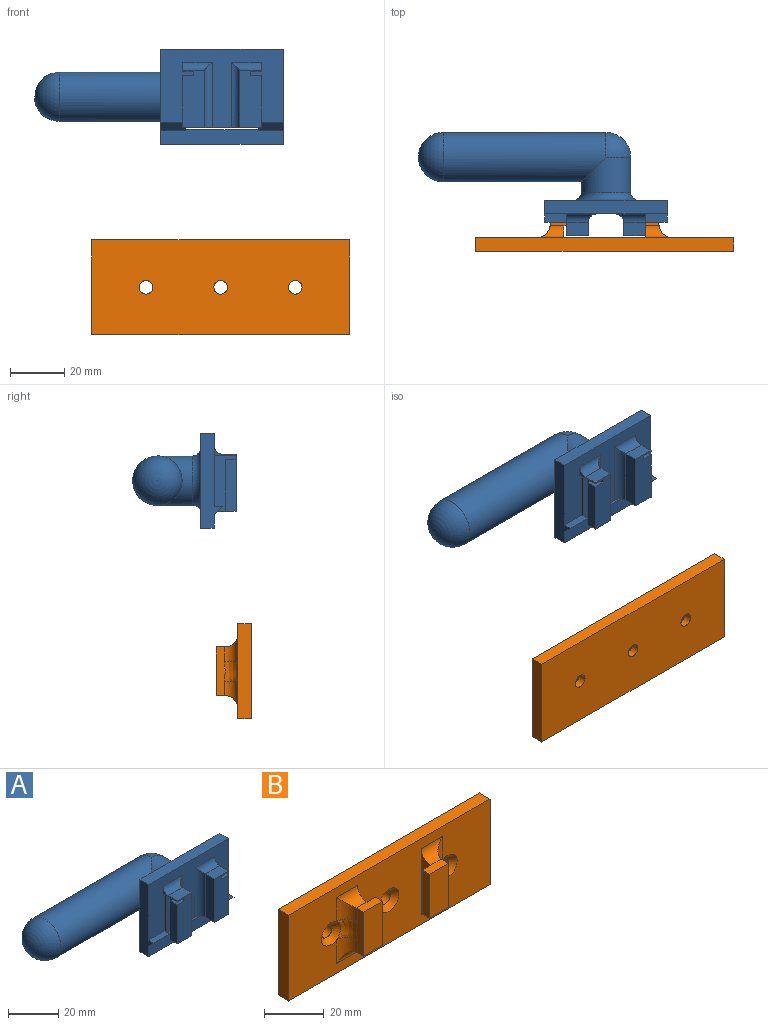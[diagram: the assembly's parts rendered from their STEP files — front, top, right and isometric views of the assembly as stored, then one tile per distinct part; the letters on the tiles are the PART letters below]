
ASSEMBLY  parts=2 mates=1
PART A: 52 faces, bbox 91.7x38.2x35.1 mm
  f0: plane 45x35mm, normal (0,1,0), area 1055.3mm2, adj f9,f10,f11,f12,f15,f20,f21,f22
  f1: plane 21x8mm, normal (0,-1,0), area 162.4mm2, adj f2,f7,f15,f17,f19,f39,f40,f41
  f2: plane 8x5.1mm, normal (0,0,1), area 40.8mm2, adj f1,f17,f41,f50
  f3: plane 19x4mm, normal (1,0,0), area 76mm2, adj f4,f15,f16,f36
  f4: plane 19x4mm, normal (0,1,0), area 76mm2, adj f3,f8,f15,f36
  f5: plane 45x5.75mm, normal (0,-1,0), area 232.2mm2, adj f9,f10,f12,f20,f27,f28,f29,f30
  f6: plane 45x28.75mm, normal (0,-1,0), area 859.3mm2, adj f7,f8,f10,f11,f12,f15,f20,f21
  f7: plane 20.4x8.1mm, normal (-1,0,0), area 89.2mm2, adj f1,f6,f15,f18,f39,f40
  f8: plane 20.45x8.1mm, normal (1,0,0), area 89.6mm2, adj f4,f6,f15,f16,f36,f37
  f9: plane 45x5mm, normal (0,0,-1), area 225mm2, adj f0,f5,f10,f12
  f10: plane 35x8mm, normal (1,0,0), area 179.5mm2, adj f0,f5,f6,f9,f11,f33,f34
  f11: plane 45x5mm, normal (0,0,1), area 225mm2, adj f0,f6,f10,f12
  f12: plane 35x8mm, normal (-1,0,0), area 179.5mm2, adj f0,f5,f6,f9,f11,f31,f32,f35
  f13: plane 8x5.1mm, normal (0,0,1), area 40.8mm2, adj f14,f16,f38,f48
  f14: plane 21x5.1mm, normal (-1,0,0), area 107.1mm2, adj f13,f15,f16,f49
  f15: plane 29.09x13.19mm, normal (0,0,-1), area 220.7mm2, adj f0,f1,f3,f4,f6,f7,f8,f14
  f16: plane 21x8mm, normal (0,-1,0), area 162.2mm2, adj f3,f8,f13,f14,f15,f36,f37,f38
  f17: plane 21x5.1mm, normal (1,0,0), area 107.1mm2, adj f1,f2,f15,f51
  f18: plane 19x4mm, normal (0,1,0), area 76mm2, adj f7,f15,f19,f39
  f19: plane 19x4mm, normal (-1,0,0), area 76mm2, adj f1,f15,f18,f39
  f20: plane 19.73x8mm, normal (-1,0,0), area 99.5mm2, adj f0,f5,f6,f21,f30,f33,f34
  f21: cylinder r=0.5mm len=5mm, axis (0,-1,0), area 7.9mm2, adj f0,f6,f20,f22
  f22: plane 18x5mm, normal (1,0,0), area 90mm2, adj f0,f6,f21,f23
  f23: cylinder r=0.5mm len=5mm, axis (0,-1,0), area 3.9mm2, adj f0,f6,f15,f22
  f24: cylinder r=0.5mm len=5mm, axis (0,-1,0), area 3.9mm2, adj f0,f6,f15,f25
  f25: plane 18x5mm, normal (-1,0,0), area 90mm2, adj f0,f6,f24,f26
  f26: cylinder r=0.5mm len=5mm, axis (0,-1,0), area 7.9mm2, adj f0,f6,f25,f27
  f27: plane 19.74x8mm, normal (1,0,0), area 99.5mm2, adj f0,f5,f6,f26,f28,f31,f32,f35
  f28: cylinder r=0.5mm len=5mm, axis (0,-1,0), area 3.9mm2, adj f0,f5,f27,f29
  f29: plane 26x5mm, normal (0,0,1), area 130mm2, adj f0,f5,f28,f30
  f30: cylinder r=0.5mm len=5mm, axis (0,-1,0), area 3.9mm2, adj f0,f5,f20,f29
  f31: plane 9x3mm, normal (0,0,1), area 27mm2, adj f6,f12,f27,f32
  f32: plane 9x0.01mm, normal (0,-1,0), area 0.1mm2, adj f12,f27,f31,f35
  f33: plane 9x3mm, normal (0,0,1), area 27mm2, adj f6,f10,f20,f34
  f34: plane 9x3mm, normal (0,-0.71,-0.71), area 38.2mm2, adj f5,f10,f20,f33
  f35: plane 9x3mm, normal (0,-0.71,-0.71), area 38.2mm2, adj f5,f12,f27,f32
  f36: plane 4x4mm, normal (0,0,1), area 16mm2, adj f3,f4,f8,f16
  f37: plane 8.1x4mm, normal (0,0,-1), area 32.4mm2, adj f6,f8,f16,f38
  f38: plane 8.1x3.55mm, normal (1,0,0), area 6.4mm2, adj f6,f13,f16,f37,f48
  f39: plane 4x4mm, normal (0,0,1), area 16mm2, adj f1,f7,f18,f19
  f40: plane 8.1x4mm, normal (0,0,-1), area 32.4mm2, adj f1,f6,f7,f41
  f41: plane 8.1x3.6mm, normal (-1,0,0), area 6.8mm2, adj f1,f2,f6,f40,f50
  f42: sphere r=9.1mm, area 260.2mm2, adj f43,f44
  f43: cylinder r=9.1mm len=18.2mm, axis (0,-1,0), area 572.4mm2, adj f42,f44,f46,f47
  f44: cylinder r=9.1mm len=60mm, axis (1,0,0), area 3265mm2, adj f42,f43,f45
  f45: sphere r=9.1mm, area 520.3mm2, adj f44
  f46: torus R=12.1mm, axis (0,-1,0), area 265.5mm2, adj f0,f43,f47
  f47: bspline ~10.45x3.38mm, area 31.1mm2, adj f15,f43,f46
  f48: cylinder r=3mm len=11mm, axis (-1,0,0), area 42.8mm2, adj f6,f13,f38,f49
  f49: cylinder r=3mm len=24mm, axis (0,0,-1), area 104.1mm2, adj f6,f14,f15,f48
  f50: cylinder r=3mm len=11mm, axis (-1,0,0), area 42.8mm2, adj f2,f6,f41,f51
  f51: cylinder r=3mm len=24mm, axis (0,0,1), area 104.1mm2, adj f6,f15,f17,f50
PART B: 36 faces, bbox 95x13x35 mm
  f0: plane 18x9mm, normal (0,-1,0), area 162mm2, adj f7,f9,f29,f31
  f1: plane 18x3.4mm, normal (1,0,0), area 61.2mm2, adj f4,f6,f28,f30
  f2: plane 27x4.6mm, normal (1,0,0), area 91.5mm2, adj f4,f12,f28,f30,f33,f35
  f3: plane 18x3.42mm, normal (-1,0,0), area 55.5mm2, adj f5,f6,f26,f27,f28,f30
  f4: plane 18x4mm, normal (0,1,0), area 72mm2, adj f1,f2,f28,f30
  f5: cylinder r=5mm len=9.76mm, axis (0,0,-1), area 53.4mm2, adj f3,f12,f27,f30,f33
  f6: plane 18x9mm, normal (0,-1,0), area 162mm2, adj f1,f3,f28,f30
  f7: plane 18x3.5mm, normal (-1,0,0), area 63mm2, adj f0,f10,f29,f31
  f8: plane 27x4.5mm, normal (-1,0,0), area 89.7mm2, adj f10,f12,f32,f34
  f9: plane 18x3.42mm, normal (1,0,0), area 55.5mm2, adj f0,f11,f24,f25,f29,f31
  f10: plane 18x4mm, normal (0,1,0), area 72mm2, adj f7,f8,f29,f31
  f11: cylinder r=5mm len=9.76mm, axis (0,0,1), area 53.4mm2, adj f9,f12,f25,f29,f34
  f12: plane 95x35mm, normal (0,-1,0), area 2615.2mm2, adj f2,f5,f8,f11,f13,f14,f15,f19
  f13: plane 35x5mm, normal (1,0,0), area 175mm2, adj f12,f14,f19,f20
  f14: plane 95x5mm, normal (0,0,1), area 475mm2, adj f12,f13,f15,f20
  f15: plane 35x5mm, normal (-1,0,0), area 175mm2, adj f12,f14,f19,f20
  f16: cylinder r=2.5mm len=5mm, axis (0,-1,0), area 47.1mm2, adj f20,f22
  f17: cylinder r=2.5mm len=5mm, axis (0,-1,0), area 47.1mm2, adj f20,f23
  f18: cylinder r=2.5mm len=5mm, axis (0,-1,0), area 47.1mm2, adj f20,f21
  f19: plane 95x5mm, normal (0,0,-1), area 475mm2, adj f12,f13,f15,f20
  f20: plane 95x35mm, normal (0,1,0), area 3266.1mm2, adj f13,f14,f15,f16,f17,f18,f19
  f21: cone r=2.5mm half-angle=45deg, axis (0,-1,0), area 62.2mm2, adj f12,f18
  f22: cone r=2.5mm half-angle=45deg, axis (0,-1,0), area 62.2mm2, adj f12,f16,f25
  f23: cone r=2.5mm half-angle=45deg, axis (0,-1,0), area 62.2mm2, adj f12,f17,f27
  f24: cylinder r=5mm len=9.76mm, axis (0,0,1), area 53.4mm2, adj f9,f12,f25,f31,f32
  f25: bspline ~8.33x5.21mm, area 48.4mm2, adj f9,f11,f22,f24
  f26: cylinder r=5mm len=9.76mm, axis (0,0,-1), area 53.4mm2, adj f3,f12,f27,f28,f35
  f27: bspline ~8.33x5.21mm, area 48.4mm2, adj f3,f5,f23,f26
  f28: plane 9.03x3.5mm, normal (0,0,1), area 31.1mm2, adj f1,f2,f3,f4,f6,f26,f35
  f29: plane 9.03x3.5mm, normal (0,0,1), area 31.5mm2, adj f0,f7,f9,f10,f11,f34
  f30: plane 9.03x3.5mm, normal (0,0,-1), area 31.1mm2, adj f1,f2,f3,f4,f5,f6,f33
  f31: plane 9.03x3.5mm, normal (0,0,-1), area 31.5mm2, adj f0,f7,f9,f10,f24,f32
  f32: cylinder r=4.5mm len=10mm, axis (1,0,0), area 48.9mm2, adj f8,f12,f24,f31
  f33: cylinder r=4.5mm len=10mm, axis (1,0,0), area 48.9mm2, adj f2,f5,f12,f30
  f34: cylinder r=4.5mm len=10mm, axis (-1,0,0), area 48.9mm2, adj f8,f11,f12,f29
  f35: cylinder r=4.5mm len=10mm, axis (-1,0,0), area 48.9mm2, adj f2,f12,f26,f28
PLACE A t=(33.85,-39.34,99.56)mm
PLACE B rot(axis=(0,0,1),180deg) t=(33.35,-53.04,29.31)mm
MATE slider A.f15 <-> B.f28  axis (0,0,-1) through (46.35,-48.44,88.31)mm
